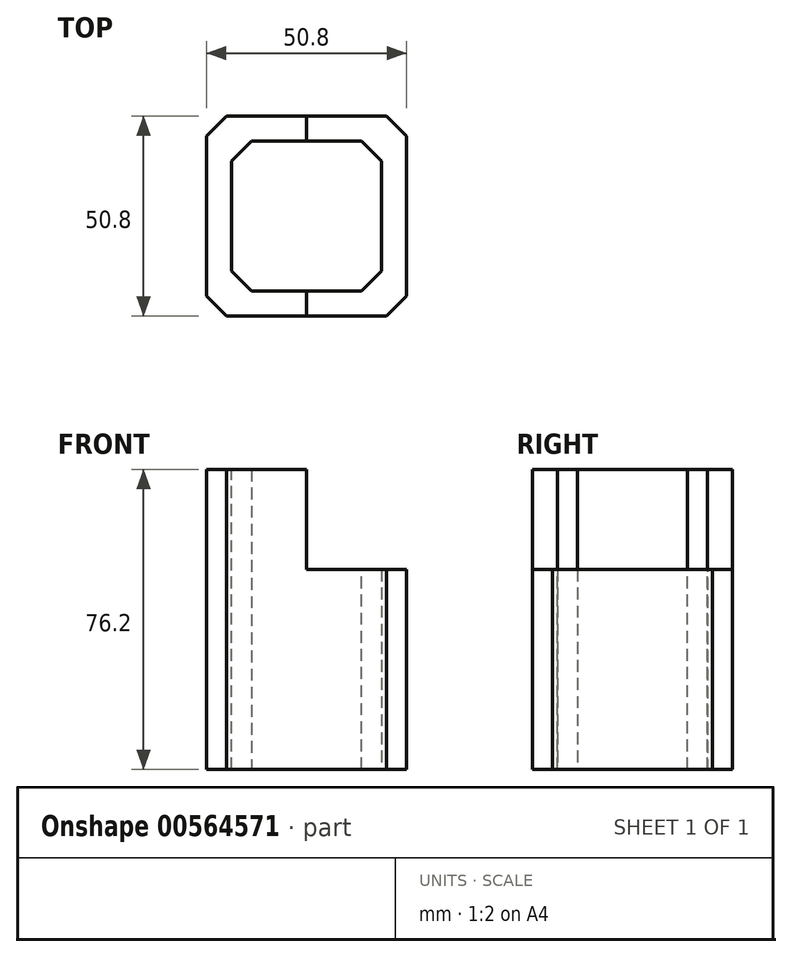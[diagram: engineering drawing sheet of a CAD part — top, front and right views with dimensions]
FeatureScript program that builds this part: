
annotation { "Feature Type Name" : "Feature", "Feature Type Description" : "" }
export const myFeature = defineFeature(function(context is Context, id is Id, definition is map)
    precondition{}
    {
        {
            var Q0;
            Q0=qCreatedBy(makeId("Front.planeOp"),FACE);
            var sketch = newSketch(context, id + "F0", { "sketchPlane" : qUnion([Q0])});
            skLineSegment(sketch, "E0", {"start": v(-25.4, 38.1) * mm, "end": v(0, 38.1) * mm});
            skLineSegment(sketch, "E1", {"start": v(0, 38.1) * mm, "end": v(0, 12.7) * mm});
            skLineSegment(sketch, "E2", {"start": v(0, 12.7) * mm, "end": v(25.4, 12.7) * mm});
            skLineSegment(sketch, "E3", {"start": v(25.4, 12.7) * mm, "end": v(25.4, -38.1) * mm});
            skLineSegment(sketch, "E4", {"start": v(25.4, -38.1) * mm, "end": v(-25.4, -38.1) * mm});
            skLineSegment(sketch, "E5", {"start": v(-25.4, -38.1) * mm, "end": v(-25.4, 38.1) * mm});
            skSolve(sketch);
        }
        {
            var Q0;
            Q0=makeQuery(id+"F0.imprint","IMPRINT",FACE,{"disambiguationData":[TD([[makeQuery(id+"F0.imprint","IMPRINT",EDGE,{"derivedFrom":sQuery(id+"F0.wireOp",EDGE,"E0")}),-1.0]])]});
            extrude(context, id + "F1", {"entities" : qUnion([Q0]), "endBound" : BoundingType.SYMMETRIC, "depth" : 50.8 * mm, "offsetDistance" : 25.4 * mm});
        }
        {
            var Q0;
            Q0=makeQuery(id+"F1.opExtrude","SWEPT_FACE",FACE,{"disambiguationData":[OSD([sQuery(id+"F0.wireOp",EDGE,"E0")])]});
            var sketch = newSketch(context, id + "F2", { "sketchPlane" : qUnion([Q0])});
            skLineSegment(sketch, "E6.bottom", {"start": v(-19.05, 19.05) * mm, "end": v(19.05, 19.05) * mm});
            skLineSegment(sketch, "E6.top", {"start": v(-19.05, -19.05) * mm, "end": v(19.05, -19.05) * mm});
            skLineSegment(sketch, "E6.left", {"start": v(-19.05, 19.05) * mm, "end": v(-19.05, -19.05) * mm});
            skLineSegment(sketch, "E6.right", {"start": v(19.05, 19.05) * mm, "end": v(19.05, -19.05) * mm});
            skSolve(sketch);
        }
        {
            var Q0;
            Q0 = qSketchRegion(id + "F2", true);
            var Q1;
            Q1=makeQuery(id+"F1.opExtrude","SWEPT_FACE",FACE,{"disambiguationData":[OSD([sQuery(id+"F0.wireOp",EDGE,"E4")])]});
            extrude(context, id + "F3", {"entities" : qUnion([Q0]), "operationType" : NewBodyOperationType.REMOVE, "endBound" : BoundingType.UP_TO_SURFACE, "oppositeDirection" : true, "depth" : 25.4 * mm, "endBoundEntityFace" : qUnion([Q1]), "offsetDistance" : 25.4 * mm});
        }
        {
            var Q0;
            Q0=makeQuery(id+"F3.boolean.opBoolean","COPY",EDGE,{"derivedFrom":makeQuery(id+"F3.opExtrude","SWEPT_EDGE",EDGE,{"disambiguationData":[OSD([sQuery(id+"F2.wireOp",EDGE,"E6.top"),sQuery(id+"F2.wireOp",EDGE,"E6.left")])]})});
            var Q1;
            Q1=makeQuery(id+"F3.boolean.opBoolean","COPY",EDGE,{"derivedFrom":makeQuery(id+"F3.opExtrude","SWEPT_EDGE",EDGE,{"disambiguationData":[OSD([sQuery(id+"F2.wireOp",EDGE,"E6.top"),sQuery(id+"F2.wireOp",EDGE,"E6.right")])]})});
            var Q2;
            Q2=makeQuery(id+"F3.boolean.opBoolean","COPY",EDGE,{"derivedFrom":makeQuery(id+"F3.opExtrude","SWEPT_EDGE",EDGE,{"disambiguationData":[OSD([sQuery(id+"F2.wireOp",EDGE,"E6.bottom"),sQuery(id+"F2.wireOp",EDGE,"E6.right")])]})});
            var Q3;
            Q3=makeQuery(id+"F3.boolean.opBoolean","COPY",EDGE,{"derivedFrom":makeQuery(id+"F3.opExtrude","SWEPT_EDGE",EDGE,{"disambiguationData":[OSD([sQuery(id+"F2.wireOp",EDGE,"E6.bottom"),sQuery(id+"F2.wireOp",EDGE,"E6.left")])]})});
            var Q4;
            Q4=makeQuery(id+"F1.opExtrude","CAP_EDGE",EDGE,{"disambiguationData":[OSD([sQuery(id+"F0.wireOp",EDGE,"E3")])],"isStart":false});
            var Q5;
            Q5=makeQuery(id+"F1.opExtrude","CAP_EDGE",EDGE,{"disambiguationData":[OSD([sQuery(id+"F0.wireOp",EDGE,"E3")])],"isStart":true});
            var Q6;
            Q6=makeQuery(id+"F1.opExtrude","CAP_EDGE",EDGE,{"disambiguationData":[OSD([sQuery(id+"F0.wireOp",EDGE,"E5")])],"isStart":true});
            var Q7;
            Q7=makeQuery(id+"F1.opExtrude","CAP_EDGE",EDGE,{"disambiguationData":[OSD([sQuery(id+"F0.wireOp",EDGE,"E5")])],"isStart":false});
            chamfer(context, id + "F4", {"entities" : qUnion([Q0, Q1, Q2, Q3, Q4, Q5, Q6, Q7]), "width" : 5.08 * mm, "tangentPropagation" : true});
        }
    });
